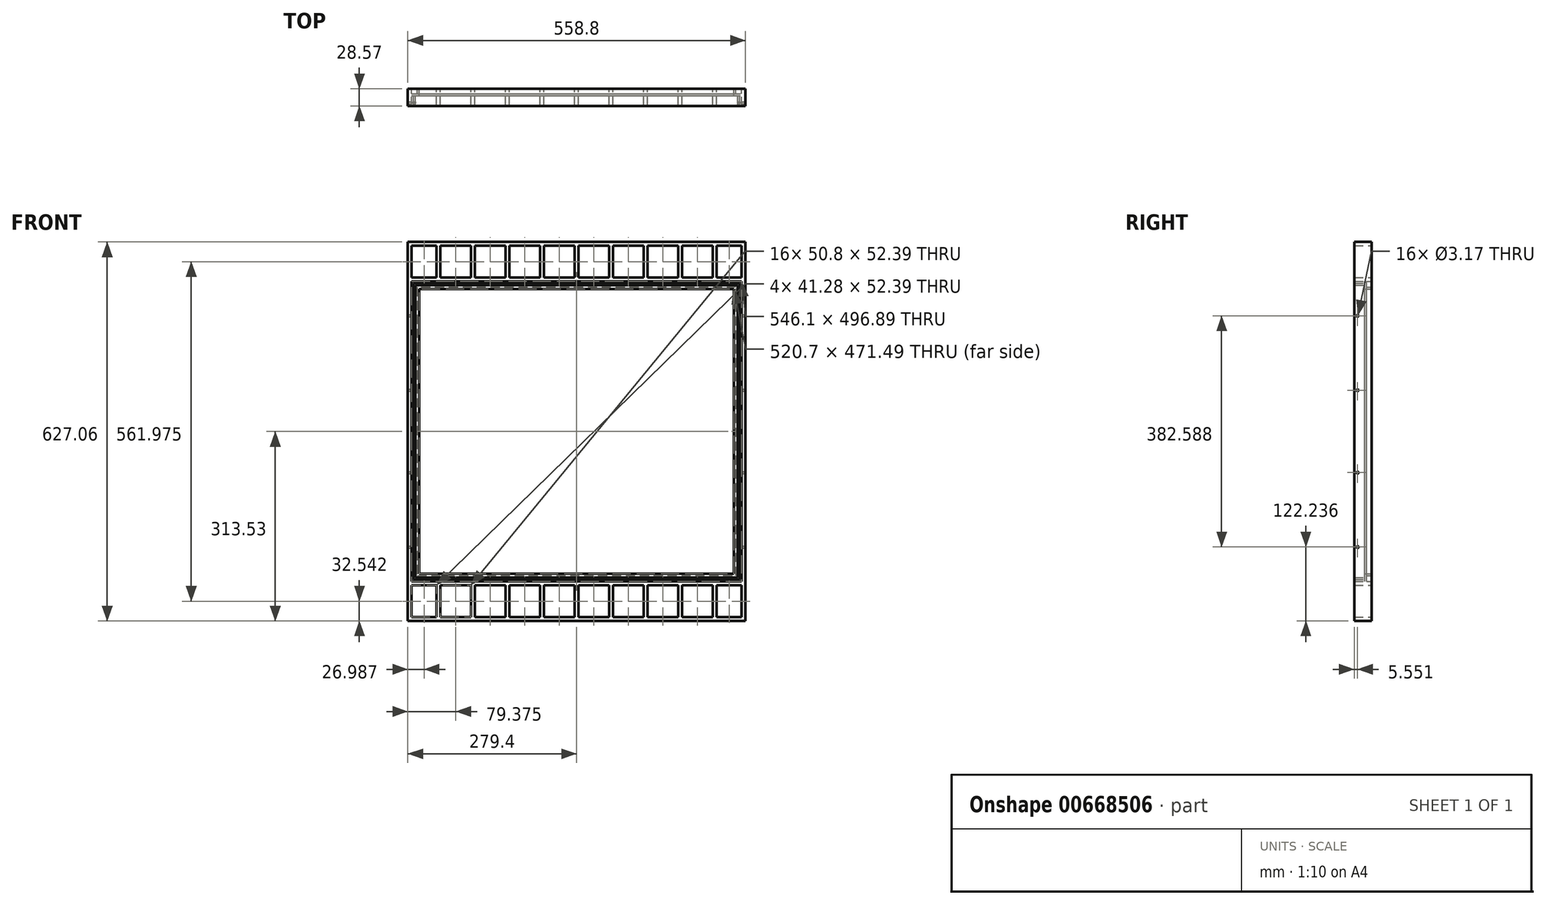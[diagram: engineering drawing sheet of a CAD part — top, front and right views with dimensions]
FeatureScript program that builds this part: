
annotation { "Feature Type Name" : "Feature", "Feature Type Description" : "" }
export const myFeature = defineFeature(function(context is Context, id is Id, definition is map)
    precondition{}
    {
        {
            var Q0;
            Q0=qCreatedBy(makeId("Front.planeOp"),FACE);
            var sketch = newSketch(context, id + "F0", { "sketchPlane" : qUnion([Q0])});
            skLineSegment(sketch, "E0.bottom", {"start": v(-279.4, -313.53) * mm, "end": v(279.4, -313.53) * mm});
            skLineSegment(sketch, "E0.top", {"start": v(-279.4, 313.53) * mm, "end": v(279.4, 313.53) * mm});
            skLineSegment(sketch, "E0.left", {"start": v(-279.4, -313.53) * mm, "end": v(-279.4, 313.53) * mm});
            skLineSegment(sketch, "E0.right", {"start": v(279.4, -313.53) * mm, "end": v(279.4, 313.53) * mm});
            skPoint(sketch, "E0.middle", {"position": v(0, 0) * mm});
            skLineSegment(sketch, "E1.0", {"start": v(-273.05, 307.18) * mm, "end": v(273.05, 307.18) * mm});
            skLineSegment(sketch, "E1.1", {"start": v(-273.05, -307.18) * mm, "end": v(-273.05, 307.18) * mm});
            skLineSegment(sketch, "E1.2", {"start": v(-273.05, -307.18) * mm, "end": v(273.05, -307.18) * mm});
            skLineSegment(sketch, "E1.3", {"start": v(273.05, -307.18) * mm, "end": v(273.05, 307.18) * mm});
            skLineSegment(sketch, "E2", {"start": v(-273.05, -254.8) * mm, "end": v(273.05, -254.8) * mm});
            skLineSegment(sketch, "E3.0", {"start": v(-273.05, -248.44) * mm, "end": v(273.05, -248.44) * mm});
            skLineSegment(sketch, "E4", {"start": v(-231.77, -254.8) * mm, "end": v(-231.77, -307.18) * mm});
            skLineSegment(sketch, "E5", {"start": v(-273.05, 254.8) * mm, "end": v(273.05, 254.8) * mm});
            skLineSegment(sketch, "E6.0", {"start": v(-273.05, 248.44) * mm, "end": v(273.05, 248.44) * mm});
            skLineSegment(sketch, "E7", {"start": v(-231.78, 254.8) * mm, "end": v(-231.78, 307.18) * mm});
            skLineSegment(sketch, "E8.0", {"start": v(-225.43, -254.8) * mm, "end": v(-225.43, -307.18) * mm});
            skLineSegment(sketch, "E9.0", {"start": v(-174.63, -254.8) * mm, "end": v(-174.63, -307.18) * mm});
            skLineSegment(sketch, "E10.0", {"start": v(-168.27, -254.8) * mm, "end": v(-168.27, -307.18) * mm});
            skLineSegment(sketch, "E11.0", {"start": v(-117.47, -254.8) * mm, "end": v(-117.47, -307.18) * mm});
            skLineSegment(sketch, "E12.0", {"start": v(-111.12, -254.8) * mm, "end": v(-111.12, -307.18) * mm});
            skLineSegment(sketch, "E13.0", {"start": v(-60.32, -254.8) * mm, "end": v(-60.32, -307.18) * mm});
            skLineSegment(sketch, "E14.0", {"start": v(-53.97, -254.8) * mm, "end": v(-53.97, -307.18) * mm});
            skLineSegment(sketch, "E15.0", {"start": v(-3.17, -254.8) * mm, "end": v(-3.17, -307.18) * mm});
            skLineSegment(sketch, "E16.0", {"start": v(3.17, -254.8) * mm, "end": v(3.17, -307.18) * mm});
            skLineSegment(sketch, "E17.0", {"start": v(53.97, -254.8) * mm, "end": v(53.97, -307.18) * mm});
            skLineSegment(sketch, "E18.0", {"start": v(60.32, -254.8) * mm, "end": v(60.32, -307.18) * mm});
            skLineSegment(sketch, "E19.0", {"start": v(111.12, -254.8) * mm, "end": v(111.12, -307.18) * mm});
            skLineSegment(sketch, "E20.0", {"start": v(117.48, -254.8) * mm, "end": v(117.48, -307.18) * mm});
            skLineSegment(sketch, "E21.0", {"start": v(168.28, -254.8) * mm, "end": v(168.28, -307.18) * mm});
            skLineSegment(sketch, "E22.0", {"start": v(174.63, -254.8) * mm, "end": v(174.63, -307.18) * mm});
            skLineSegment(sketch, "E23.0", {"start": v(225.43, -254.8) * mm, "end": v(225.43, -307.18) * mm});
            skLineSegment(sketch, "E24.0", {"start": v(231.78, -254.8) * mm, "end": v(231.78, -307.18) * mm});
            skLineSegment(sketch, "E25", {"start": v(-225.43, 307.18) * mm, "end": v(-225.43, 254.8) * mm});
            skLineSegment(sketch, "E26", {"start": v(-174.63, 307.18) * mm, "end": v(-174.63, 254.8) * mm});
            skLineSegment(sketch, "E27", {"start": v(-168.28, 307.18) * mm, "end": v(-168.28, 254.8) * mm});
            skLineSegment(sketch, "E28", {"start": v(-117.48, 307.18) * mm, "end": v(-117.48, 254.8) * mm});
            skLineSegment(sketch, "E29", {"start": v(-111.13, 307.18) * mm, "end": v(-111.13, 254.8) * mm});
            skLineSegment(sketch, "E30", {"start": v(-60.33, 307.18) * mm, "end": v(-60.33, 254.8) * mm});
            skLineSegment(sketch, "E31", {"start": v(-53.98, 307.18) * mm, "end": v(-53.98, 254.8) * mm});
            skLineSegment(sketch, "E32", {"start": v(-3.18, 307.18) * mm, "end": v(-3.18, 254.8) * mm});
            skLineSegment(sketch, "E33", {"start": v(3.17, 307.18) * mm, "end": v(3.17, 254.8) * mm});
            skLineSegment(sketch, "E34", {"start": v(53.97, 307.18) * mm, "end": v(53.97, 254.8) * mm});
            skLineSegment(sketch, "E35", {"start": v(60.32, 307.18) * mm, "end": v(60.32, 254.8) * mm});
            skLineSegment(sketch, "E36", {"start": v(111.12, 307.18) * mm, "end": v(111.12, 254.8) * mm});
            skLineSegment(sketch, "E37", {"start": v(117.47, 307.18) * mm, "end": v(117.47, 254.8) * mm});
            skLineSegment(sketch, "E38", {"start": v(168.27, 307.18) * mm, "end": v(168.27, 254.8) * mm});
            skLineSegment(sketch, "E39", {"start": v(174.62, 307.18) * mm, "end": v(174.62, 254.8) * mm});
            skLineSegment(sketch, "E40", {"start": v(225.42, 307.18) * mm, "end": v(225.42, 254.8) * mm});
            skLineSegment(sketch, "E41", {"start": v(231.77, 307.18) * mm, "end": v(231.77, 254.8) * mm});
            skSolve(sketch);
        }
        {
            var Q0;
            Q0 = qSketchRegion(id + "F0", true);
            var Q1;
            {var subQ0=sQuery(id+"F0.wireOp",EDGE,"E7");Q1=makeQuery(id+"F0.imprint","IMPRINT",FACE,{"disambiguationData":[TD([[makeQuery(id+"F0.imprint","IMPRINT",EDGE,{"derivedFrom":subQ0}),-1.0]])]});}
            var Q2;
            {var subQ0=sQuery(id+"F0.wireOp",EDGE,"E26");Q2=makeQuery(id+"F0.imprint","IMPRINT",FACE,{"disambiguationData":[TD([[makeQuery(id+"F0.imprint","IMPRINT",EDGE,{"derivedFrom":subQ0}),1.0]])]});}
            var Q3;
            {var subQ0=sQuery(id+"F0.wireOp",EDGE,"E28");Q3=makeQuery(id+"F0.imprint","IMPRINT",FACE,{"disambiguationData":[TD([[makeQuery(id+"F0.imprint","IMPRINT",EDGE,{"derivedFrom":subQ0}),1.0]])]});}
            var Q4;
            {var subQ0=sQuery(id+"F0.wireOp",EDGE,"E30");Q4=makeQuery(id+"F0.imprint","IMPRINT",FACE,{"disambiguationData":[TD([[makeQuery(id+"F0.imprint","IMPRINT",EDGE,{"derivedFrom":subQ0}),1.0]])]});}
            var Q5;
            {var subQ0=sQuery(id+"F0.wireOp",EDGE,"E32");Q5=makeQuery(id+"F0.imprint","IMPRINT",FACE,{"disambiguationData":[TD([[makeQuery(id+"F0.imprint","IMPRINT",EDGE,{"derivedFrom":subQ0}),1.0]])]});}
            var Q6;
            {var subQ0=sQuery(id+"F0.wireOp",EDGE,"E34");Q6=makeQuery(id+"F0.imprint","IMPRINT",FACE,{"disambiguationData":[TD([[makeQuery(id+"F0.imprint","IMPRINT",EDGE,{"derivedFrom":subQ0}),1.0]])]});}
            var Q7;
            {var subQ10=sQuery(id+"F0.wireOp",EDGE,"E6.0");Q7=makeQuery(id+"F0.imprint","IMPRINT",FACE,{"disambiguationData":[TD([[makeQuery(id+"F0.imprint","IMPRINT",EDGE,{"derivedFrom":subQ10}),1.0]])]});}
            var Q8;
            {var subQ0=sQuery(id+"F0.wireOp",EDGE,"E36");Q8=makeQuery(id+"F0.imprint","IMPRINT",FACE,{"disambiguationData":[TD([[makeQuery(id+"F0.imprint","IMPRINT",EDGE,{"derivedFrom":subQ0}),1.0]])]});}
            var Q9;
            {var subQ0=sQuery(id+"F0.wireOp",EDGE,"E38");Q9=makeQuery(id+"F0.imprint","IMPRINT",FACE,{"disambiguationData":[TD([[makeQuery(id+"F0.imprint","IMPRINT",EDGE,{"derivedFrom":subQ0}),1.0]])]});}
            var Q10;
            {var subQ9=sQuery(id+"F0.wireOp",EDGE,"E3.0");Q10=makeQuery(id+"F0.imprint","IMPRINT",FACE,{"disambiguationData":[TD([[makeQuery(id+"F0.imprint","IMPRINT",EDGE,{"derivedFrom":subQ9}),-1.0]])]});}
            var Q11;
            {var subQ0=sQuery(id+"F0.wireOp",EDGE,"E11.0");Q11=makeQuery(id+"F0.imprint","IMPRINT",FACE,{"disambiguationData":[TD([[makeQuery(id+"F0.imprint","IMPRINT",EDGE,{"derivedFrom":subQ0}),1.0]])]});}
            var Q12;
            {var subQ0=sQuery(id+"F0.wireOp",EDGE,"E9.0");Q12=makeQuery(id+"F0.imprint","IMPRINT",FACE,{"disambiguationData":[TD([[makeQuery(id+"F0.imprint","IMPRINT",EDGE,{"derivedFrom":subQ0}),1.0]])]});}
            var Q13;
            {var subQ0=sQuery(id+"F0.wireOp",EDGE,"E4");Q13=makeQuery(id+"F0.imprint","IMPRINT",FACE,{"disambiguationData":[TD([[makeQuery(id+"F0.imprint","IMPRINT",EDGE,{"derivedFrom":subQ0}),1.0]])]});}
            var Q14;
            {var subQ0=sQuery(id+"F0.wireOp",EDGE,"E13.0");Q14=makeQuery(id+"F0.imprint","IMPRINT",FACE,{"disambiguationData":[TD([[makeQuery(id+"F0.imprint","IMPRINT",EDGE,{"derivedFrom":subQ0}),1.0]])]});}
            var Q15;
            {var subQ0=sQuery(id+"F0.wireOp",EDGE,"E15.0");Q15=makeQuery(id+"F0.imprint","IMPRINT",FACE,{"disambiguationData":[TD([[makeQuery(id+"F0.imprint","IMPRINT",EDGE,{"derivedFrom":subQ0}),1.0]])]});}
            var Q16;
            {var subQ0=sQuery(id+"F0.wireOp",EDGE,"E17.0");Q16=makeQuery(id+"F0.imprint","IMPRINT",FACE,{"disambiguationData":[TD([[makeQuery(id+"F0.imprint","IMPRINT",EDGE,{"derivedFrom":subQ0}),1.0]])]});}
            var Q17;
            {var subQ0=sQuery(id+"F0.wireOp",EDGE,"E19.0");Q17=makeQuery(id+"F0.imprint","IMPRINT",FACE,{"disambiguationData":[TD([[makeQuery(id+"F0.imprint","IMPRINT",EDGE,{"derivedFrom":subQ0}),1.0]])]});}
            var Q18;
            {var subQ0=sQuery(id+"F0.wireOp",EDGE,"E21.0");Q18=makeQuery(id+"F0.imprint","IMPRINT",FACE,{"disambiguationData":[TD([[makeQuery(id+"F0.imprint","IMPRINT",EDGE,{"derivedFrom":subQ0}),1.0]])]});}
            var Q19;
            {var subQ0=sQuery(id+"F0.wireOp",EDGE,"E23.0");Q19=makeQuery(id+"F0.imprint","IMPRINT",FACE,{"disambiguationData":[TD([[makeQuery(id+"F0.imprint","IMPRINT",EDGE,{"derivedFrom":subQ0}),1.0]])]});}
            var Q20;
            {var subQ0=sQuery(id+"F0.wireOp",EDGE,"E40");Q20=makeQuery(id+"F0.imprint","IMPRINT",FACE,{"disambiguationData":[TD([[makeQuery(id+"F0.imprint","IMPRINT",EDGE,{"derivedFrom":subQ0}),1.0]])]});}
            extrude(context, id + "F1", {"entities" : qUnion([Q0, Q1, Q2, Q3, Q4, Q5, Q6, Q7, Q8, Q9, Q10, Q11, Q12, Q13, Q14, Q15, Q16, Q17, Q18, Q19, Q20]), "depth" : 28.57 * mm, "offsetDistance" : 25.4 * mm});
        }
        {
            var Q0;
            Q0=makeQuery(id+"F1.opExtrude","CAP_FACE",FACE,{"disambiguationData":[OSD([sQuery(id+"F0.wireOp",EDGE,"E0.bottom"),sQuery(id+"F0.wireOp",EDGE,"E0.top"),sQuery(id+"F0.wireOp",EDGE,"E0.left"),sQuery(id+"F0.wireOp",EDGE,"E0.right"),sQuery(id+"F0.wireOp",EDGE,"E1.0"),sQuery(id+"F0.wireOp",EDGE,"E1.1"),sQuery(id+"F0.wireOp",EDGE,"E1.2"),sQuery(id+"F0.wireOp",EDGE,"E1.3"),sQuery(id+"F0.wireOp",EDGE,"E2"),sQuery(id+"F0.wireOp",EDGE,"E3.0"),sQuery(id+"F0.wireOp",EDGE,"E4"),sQuery(id+"F0.wireOp",EDGE,"E5"),sQuery(id+"F0.wireOp",EDGE,"E6.0"),sQuery(id+"F0.wireOp",EDGE,"E7"),sQuery(id+"F0.wireOp",EDGE,"E8.0"),sQuery(id+"F0.wireOp",EDGE,"E9.0"),sQuery(id+"F0.wireOp",EDGE,"E10.0"),sQuery(id+"F0.wireOp",EDGE,"E11.0"),sQuery(id+"F0.wireOp",EDGE,"E12.0"),sQuery(id+"F0.wireOp",EDGE,"E13.0"),sQuery(id+"F0.wireOp",EDGE,"E14.0"),sQuery(id+"F0.wireOp",EDGE,"E15.0"),sQuery(id+"F0.wireOp",EDGE,"E16.0"),sQuery(id+"F0.wireOp",EDGE,"E17.0"),sQuery(id+"F0.wireOp",EDGE,"E18.0"),sQuery(id+"F0.wireOp",EDGE,"E19.0"),sQuery(id+"F0.wireOp",EDGE,"E20.0"),sQuery(id+"F0.wireOp",EDGE,"E21.0"),sQuery(id+"F0.wireOp",EDGE,"E22.0"),sQuery(id+"F0.wireOp",EDGE,"E23.0"),sQuery(id+"F0.wireOp",EDGE,"E24.0"),sQuery(id+"F0.wireOp",EDGE,"E25"),sQuery(id+"F0.wireOp",EDGE,"E26"),sQuery(id+"F0.wireOp",EDGE,"E27"),sQuery(id+"F0.wireOp",EDGE,"E28"),sQuery(id+"F0.wireOp",EDGE,"E29"),sQuery(id+"F0.wireOp",EDGE,"E30"),sQuery(id+"F0.wireOp",EDGE,"E31"),sQuery(id+"F0.wireOp",EDGE,"E32"),sQuery(id+"F0.wireOp",EDGE,"E33"),sQuery(id+"F0.wireOp",EDGE,"E34"),sQuery(id+"F0.wireOp",EDGE,"E35"),sQuery(id+"F0.wireOp",EDGE,"E36"),sQuery(id+"F0.wireOp",EDGE,"E37"),sQuery(id+"F0.wireOp",EDGE,"E38"),sQuery(id+"F0.wireOp",EDGE,"E39"),sQuery(id+"F0.wireOp",EDGE,"E40"),sQuery(id+"F0.wireOp",EDGE,"E41")])],"isStart":true});
            var sketch = newSketch(context, id + "F2", { "sketchPlane" : qUnion([Q0])});
            skLineSegment(sketch, "E42", {"start": v(-273.05, 248.44) * mm, "end": v(273.05, 248.44) * mm});
            skLineSegment(sketch, "E43", {"start": v(273.05, 248.44) * mm, "end": v(273.05, -248.44) * mm});
            skLineSegment(sketch, "E44", {"start": v(273.05, -248.44) * mm, "end": v(-273.05, -248.44) * mm});
            skLineSegment(sketch, "E45", {"start": v(-273.05, -248.44) * mm, "end": v(-273.05, 248.44) * mm});
            skLineSegment(sketch, "E46.0", {"start": v(-263.53, -238.92) * mm, "end": v(-263.53, 238.92) * mm});
            skLineSegment(sketch, "E46.1", {"start": v(263.53, -238.92) * mm, "end": v(-263.53, -238.92) * mm});
            skLineSegment(sketch, "E46.2", {"start": v(263.53, 238.92) * mm, "end": v(263.52, -238.92) * mm});
            skLineSegment(sketch, "E46.3", {"start": v(-263.53, 238.92) * mm, "end": v(263.53, 238.92) * mm});
            skLineSegment(sketch, "E47.0", {"start": v(-260.35, -235.74) * mm, "end": v(-260.35, 235.74) * mm});
            skLineSegment(sketch, "E47.1", {"start": v(260.35, -235.74) * mm, "end": v(-260.35, -235.74) * mm});
            skLineSegment(sketch, "E47.2", {"start": v(260.35, 235.74) * mm, "end": v(260.35, -235.74) * mm});
            skLineSegment(sketch, "E47.3", {"start": v(-260.35, 235.74) * mm, "end": v(260.35, 235.74) * mm});
            skSolve(sketch);
        }
        {
            var Q0;
            Q0 = qSketchRegion(id + "F2", true);
            var Q1;
            Q1=makeQuery(id+"F2.imprint","IMPRINT",FACE,{"disambiguationData":[TD([[makeQuery(id+"F2.imprint","IMPRINT",EDGE,{"derivedFrom":sQuery(id+"F2.wireOp",EDGE,"E46.0")}),-1.0]])]});
            extrude(context, id + "F3", {"entities" : qUnion([Q0, Q1]), "operationType" : NewBodyOperationType.ADD, "oppositeDirection" : true, "depth" : 11.1 * mm, "offsetDistance" : 25.4 * mm});
        }
        {
            var Q0;
            Q0=makeQuery(id+"F2.imprint","IMPRINT",FACE,{"disambiguationData":[TD([[makeQuery(id+"F2.imprint","IMPRINT",EDGE,{"derivedFrom":sQuery(id+"F2.wireOp",EDGE,"E42")}),1.0]])]});
            extrude(context, id + "F4", {"entities" : qUnion([Q0]), "operationType" : NewBodyOperationType.REMOVE, "oppositeDirection" : true, "depth" : 7.94 * mm, "offsetDistance" : 25.4 * mm});
        }
        {
            var Q0;
            Q0=makeQuery(id+"F3.opExtrude","CAP_FACE",FACE,{"disambiguationData":[OSD([sQuery(id+"F2.wireOp",EDGE,"E42"),sQuery(id+"F2.wireOp",EDGE,"E43"),sQuery(id+"F2.wireOp",EDGE,"E44"),sQuery(id+"F2.wireOp",EDGE,"E45"),sQuery(id+"F2.wireOp",EDGE,"E47.0"),sQuery(id+"F2.wireOp",EDGE,"E47.1"),sQuery(id+"F2.wireOp",EDGE,"E47.2"),sQuery(id+"F2.wireOp",EDGE,"E47.3")])],"isStart":false});
            var sketch = newSketch(context, id + "F5", { "sketchPlane" : qUnion([Q0])});
            skLineSegment(sketch, "E48.0", {"start": v(-273.05, -248.44) * mm, "end": v(-273.05, 248.44) * mm});
            skLineSegment(sketch, "E49.0", {"start": v(-273.05, 248.44) * mm, "end": v(273.05, 248.44) * mm});
            skLineSegment(sketch, "E50.0", {"start": v(269.88, -245.27) * mm, "end": v(269.88, 245.27) * mm});
            skLineSegment(sketch, "E50.1", {"start": v(-269.88, -245.27) * mm, "end": v(269.88, -245.27) * mm});
            skLineSegment(sketch, "E50.2", {"start": v(-269.88, -245.27) * mm, "end": v(-269.88, 245.27) * mm});
            skLineSegment(sketch, "E50.3", {"start": v(-269.88, 245.27) * mm, "end": v(269.88, 245.27) * mm});
            skLineSegment(sketch, "E51.0", {"start": v(266.7, -242.1) * mm, "end": v(266.7, 242.1) * mm});
            skLineSegment(sketch, "E51.1", {"start": v(-266.7, -242.1) * mm, "end": v(266.7, -242.1) * mm});
            skLineSegment(sketch, "E51.2", {"start": v(-266.7, -242.1) * mm, "end": v(-266.7, 242.1) * mm});
            skLineSegment(sketch, "E51.3", {"start": v(-266.7, 242.1) * mm, "end": v(266.7, 242.1) * mm});
            skSolve(sketch);
        }
        {
            var Q0;
            Q0 = qSketchRegion(id + "F5", true);
            extrude(context, id + "F6", {"entities" : qUnion([Q0]), "operationType" : NewBodyOperationType.ADD, "depth" : 17.46 * mm, "offsetDistance" : 25.4 * mm});
        }
        {
            var Q0;
            Q0=makeQuery(id+"F6.opExtrude","SWEPT_FACE",FACE,{"disambiguationData":[OSD([sQuery(id+"F5.wireOp",EDGE,"E51.0")])]});
            var sketch = newSketch(context, id + "F7", { "sketchPlane" : qUnion([Q0])});
            skLineSegment(sketch, "E52", {"start": v(23.02, 242.1) * mm, "end": v(23.02, -242.1) * mm, "construction": true});
            skPoint(sketch, "E52.endSnap0", {"position": v(19.84, -242.1) * mm});
            skCircle(sketch, "E53", {"center": v(23.02, 191.3) * mm, "radius": 1.59 * mm});
            skCircle(sketch, "E54", {"center": v(23.02, 68.1) * mm, "radius": 1.59 * mm});
            skCircle(sketch, "E55", {"center": v(23.02, -191.3) * mm, "radius": 1.59 * mm});
            skCircle(sketch, "E56", {"center": v(23.02, -68.1) * mm, "radius": 1.59 * mm});
            skSolve(sketch);
        }
        {
            var Q0;
            Q0 = qSketchRegion(id + "F7", true);
            extrude(context, id + "F8", {"entities" : qUnion([Q0]), "operationType" : NewBodyOperationType.REMOVE, "depth" : 1524 * mm, "offsetDistance" : 25.4 * mm, "symmetric" : true});
        }
    });
